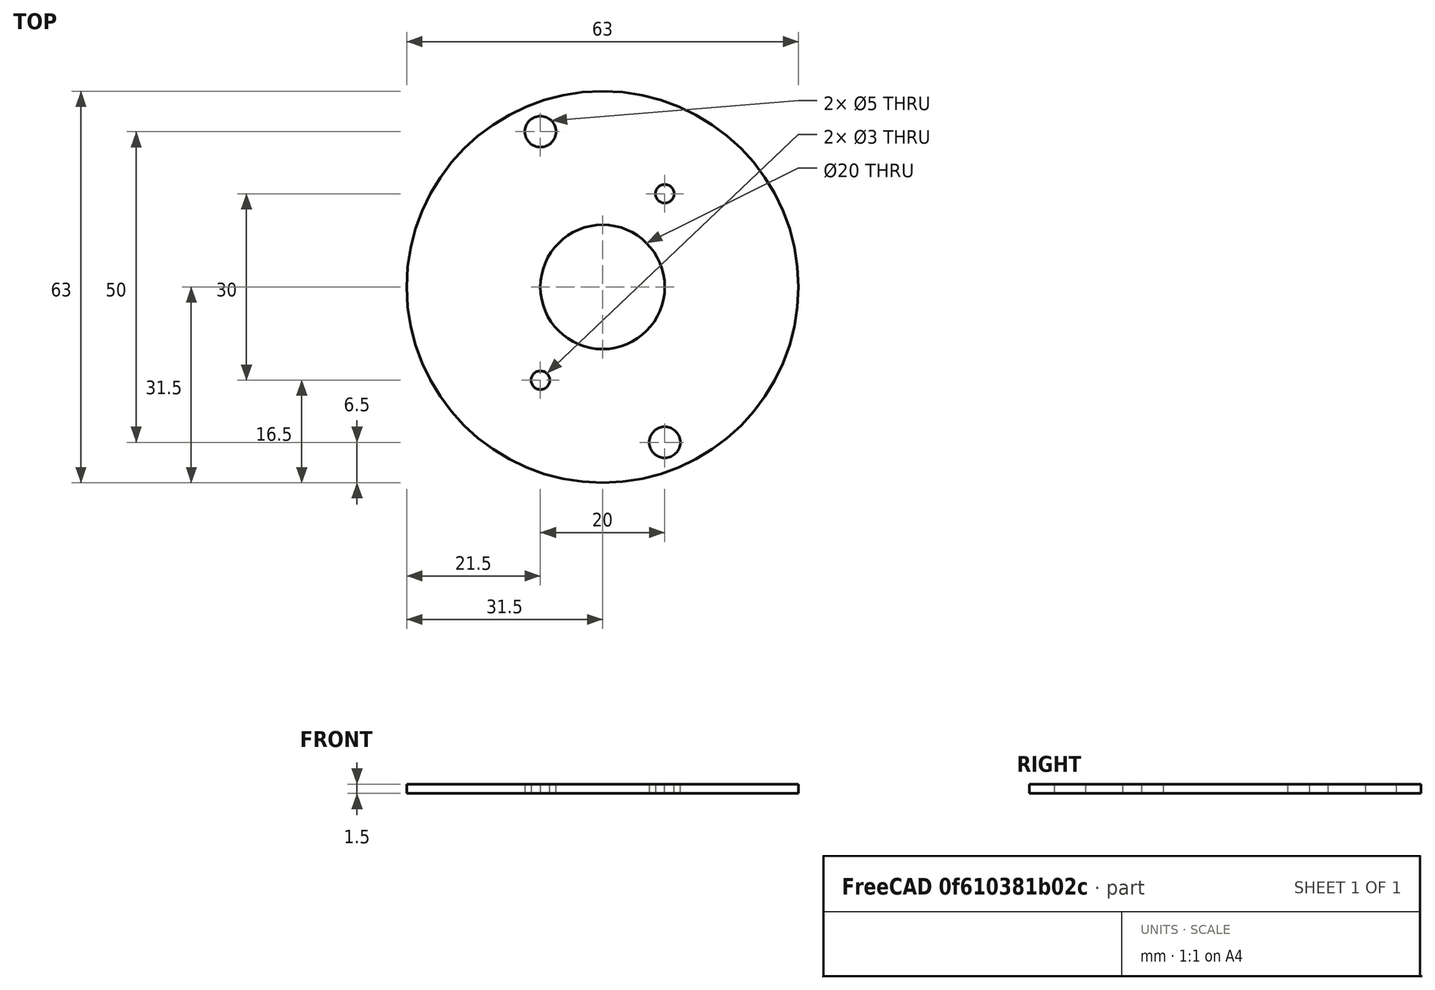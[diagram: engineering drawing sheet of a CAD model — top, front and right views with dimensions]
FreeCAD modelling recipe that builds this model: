
FCSTD DOCUMENT  (FreeCAD 0.19R24276 (Git))
Label: Mobile_connection_bottom_part_N1_add_1_5
License: All rights reserved
LicenseURL: http://en.wikipedia.org/wiki/All_rights_reserved
objects: Sketcher::SketchObject×1, PartDesign::Pad×1, PartDesign::Body×1
note: 4 computed .brp shape members not serialized (recipe doc carries the construction recipe); baked Part::Feature solids carry a one-line shape summary decoded from their .brp

FEATURE [Sketcher::SketchObject] Sketch005
  FullyConstrained = true
  MapMode = 5
  Placement = pos=(0,0,3) rot=(0,0,1;0rad)
  sketch-geometry (14):
    g0: LineSegment StartX=-10 StartY=15 StartZ=0 EndX=10 EndY=15 EndZ=0
    g1: LineSegment StartX=10 StartY=15 StartZ=0 EndX=10 EndY=-15 EndZ=0
    g2: LineSegment StartX=10 StartY=-15 StartZ=0 EndX=-10 EndY=-15 EndZ=0
    g3: LineSegment StartX=-10 StartY=-15 StartZ=0 EndX=-10 EndY=15 EndZ=0
    g4: LineSegment StartX=-10 StartY=25 StartZ=0 EndX=10 EndY=25 EndZ=0
    g5: LineSegment StartX=10 StartY=25 StartZ=0 EndX=10 EndY=-25 EndZ=0
    g6: LineSegment StartX=10 StartY=-25 StartZ=0 EndX=-10 EndY=-25 EndZ=0
    g7: LineSegment StartX=-10 StartY=-25 StartZ=0 EndX=-10 EndY=25 EndZ=0
    g8: Circle CenterX=-10 CenterY=25 CenterZ=0 NormalX=0 NormalY=0 NormalZ=1 AngleXU=0 Radius=2.5
    g9: Circle CenterX=10 CenterY=-25 CenterZ=0 NormalX=0 NormalY=0 NormalZ=1 AngleXU=0 Radius=2.5
    g10: Circle CenterX=-10 CenterY=-15 CenterZ=0 NormalX=0 NormalY=0 NormalZ=1 AngleXU=0 Radius=1.5
    g11: Circle CenterX=10 CenterY=15 CenterZ=0 NormalX=0 NormalY=0 NormalZ=1 AngleXU=0 Radius=1.5
    g12: Circle CenterX=0 CenterY=0 CenterZ=0 NormalX=0 NormalY=0 NormalZ=1 AngleXU=0 Radius=31.5
    g13: Circle CenterX=0 CenterY=0 CenterZ=0 NormalX=0 NormalY=0 NormalZ=1 AngleXU=0 Radius=10
  constraints (34):
    c: Coincident(g0,g1)
    c: Coincident(g1,g2)
    c: Coincident(g2,g3)
    c: Coincident(g3,g0)
    c: Horizontal(g0)
    c: Horizontal(g2)
    c: Vertical(g1)
    c: Vertical(g3)
    c: Symmetric(g0,g1,g-1)
    c: DistanceY(g1,g1) = 30
    c: DistanceX(g0,g0) = 20
    c: Coincident(g4,g5)
    c: Coincident(g5,g6)
    c: Coincident(g6,g7)
    c: Coincident(g7,g4)
    c: Horizontal(g4)
    c: Horizontal(g6)
    c: Vertical(g5)
    c: Vertical(g7)
    c: Symmetric(g4,g5,g-1)
    c: DistanceY(g5,g5) = 50
    c: DistanceX(g4,g4) = 20
    c: Coincident(g8,g4)
    c: Coincident(g9,g5)
    c: Coincident(g10,g2)
    c: Coincident(g11,g0)
    c: Diameter(g8) = 5
    c: Diameter(g9) = 5
    c: Diameter(g11) = 3
    c: Diameter(g10) = 3
    c: Coincident(g12,g-1)
    c: Diameter(g12) = 63
    c: Coincident(g13,g12)
    c: Diameter(g13) = 20
FEATURE [PartDesign::Pad] Pad
  Direction = (1,1,1)
  Length = 1.5
  Length2 = 100
  Placement = pos=(0,0,3) rot=(0,0,1;0rad)
  Profile = -> Sketch005
  Type = 0
FEATURE [PartDesign::Body] Body
  Group = -> [Sketch005,Pad]
  Origin = -> Origin
  Tip = -> Pad
